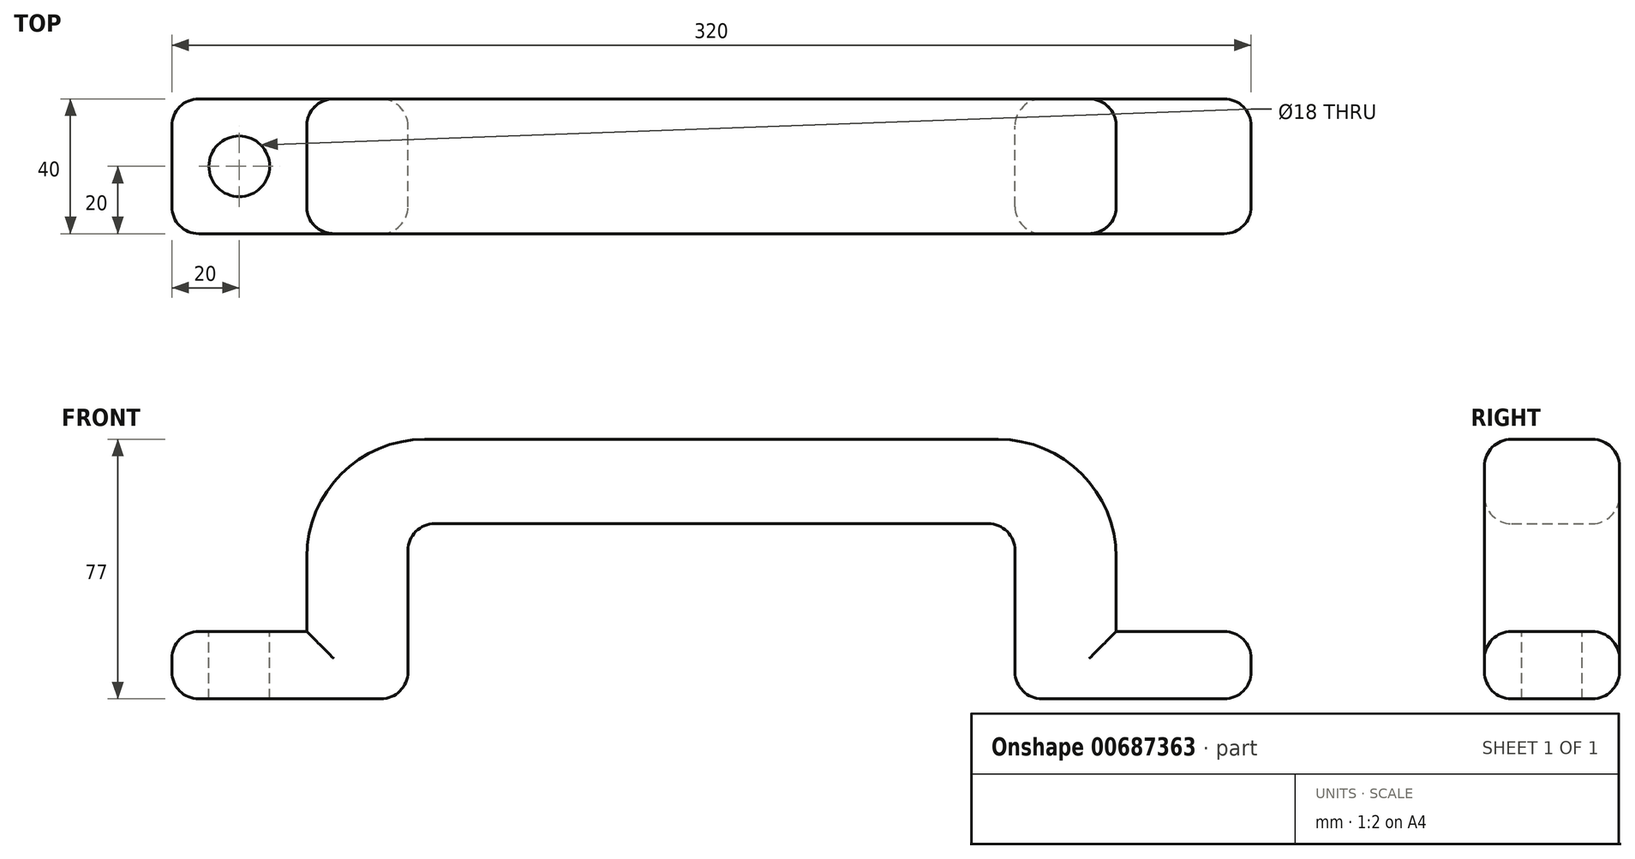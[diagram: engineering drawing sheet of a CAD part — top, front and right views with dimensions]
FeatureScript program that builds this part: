
annotation { "Feature Type Name" : "Feature", "Feature Type Description" : "" }
export const myFeature = defineFeature(function(context is Context, id is Id, definition is map)
    precondition{}
    {
        {
            var Q0;
            Q0=qCreatedBy(makeId("Front.planeOp"),FACE);
            var sketch = newSketch(context, id + "F0", { "sketchPlane" : qUnion([Q0])});
            skLineSegment(sketch, "E0.top", {"start": v(-120, 0) * mm, "end": v(-90, 0) * mm});
            skLineSegment(sketch, "E0.left", {"start": v(-120, 52) * mm, "end": v(-120, 0) * mm});
            skLineSegment(sketch, "E0.right", {"start": v(-90, 52) * mm, "end": v(-90, 0) * mm});
            skLineSegment(sketch, "E1.bottom", {"start": v(-90, 52) * mm, "end": v(0, 52) * mm});
            skLineSegment(sketch, "E1.top", {"start": v(-120, 77) * mm, "end": v(0, 77) * mm});
            skLineSegment(sketch, "E1.left", {"start": v(-120, 52) * mm, "end": v(-120, 77) * mm});
            skLineSegment(sketch, "E2.bottom", {"start": v(-120, 20) * mm, "end": v(-160, 20) * mm});
            skLineSegment(sketch, "E2.top", {"start": v(-120, 0) * mm, "end": v(-160, 0) * mm});
            skLineSegment(sketch, "E2.right", {"start": v(-160, 20) * mm, "end": v(-160, 0) * mm});
            skLineSegment(sketch, "E3.MirrorCS", {"start": v(120, 77) * mm, "end": v(0, 77) * mm});
            skLineSegment(sketch, "E4.MirrorCS", {"start": v(90, 52) * mm, "end": v(90, 0) * mm});
            skLineSegment(sketch, "E5.MirrorCS", {"start": v(120, 0) * mm, "end": v(90, 0) * mm});
            skLineSegment(sketch, "E6.MirrorCS", {"start": v(120, 0) * mm, "end": v(160, 0) * mm});
            skLineSegment(sketch, "E7.MirrorCS", {"start": v(160, 20) * mm, "end": v(160, 0) * mm});
            skLineSegment(sketch, "E8.MirrorCS", {"start": v(120, 52) * mm, "end": v(120, 20) * mm});
            skLineSegment(sketch, "E9.MirrorCS", {"start": v(120, 52) * mm, "end": v(120, 77) * mm});
            skLineSegment(sketch, "E10.MirrorCS", {"start": v(120, 20) * mm, "end": v(160, 20) * mm});
            skLineSegment(sketch, "E11.MirrorCS", {"start": v(90, 52) * mm, "end": v(0, 52) * mm});
            skPoint(sketch, "E12.orphan", {"position": v(120, 0) * mm});
            skSolve(sketch);
        }
        {
            var Q0;
            Q0 = qSketchRegion(id + "F0", true);
            extrude(context, id + "F1", {"entities" : qUnion([Q0]), "depth" : 40 * mm, "offsetDistance" : 25 * mm});
        }
        {
            var Q0;
            Q0=makeQuery(id+"F1.opExtrude","SWEPT_FACE",FACE,{"disambiguationData":[OSD([sQuery(id+"F0.wireOp",EDGE,"E2.bottom")])]});
            var sketch = newSketch(context, id + "F2", { "sketchPlane" : qUnion([Q0])});
            skCircle(sketch, "E13", {"center": v(-140, -20) * mm, "radius": 9 * mm});
            skPoint(sketch, "E13.centerSnap0", {"position": v(-140, 0) * mm});
            skPoint(sketch, "E13.centerSnap1", {"position": v(-120, -20) * mm});
            skSolve(sketch);
        }
        {
            var Q0;
            Q0 = qSketchRegion(id + "F2", true);
            extrude(context, id + "F3", {"entities" : qUnion([Q0]), "operationType" : NewBodyOperationType.REMOVE, "oppositeDirection" : true, "depth" : 74.7 * mm, "offsetDistance" : 25 * mm});
        }
        {
            var Q0;
            Q0=makeQuery(id+"F1.opExtrude","CAP_EDGE",EDGE,{"disambiguationData":[OSD([sQuery(id+"F0.wireOp",EDGE,"E2.right")])],"isStart":false});
            var Q1;
            Q1=makeQuery(id+"F1.opExtrude","CAP_EDGE",EDGE,{"disambiguationData":[OSD([sQuery(id+"F0.wireOp",EDGE,"E2.right")])],"isStart":true});
            var Q2;
            Q2=makeQuery(id+"F1.opExtrude","CAP_EDGE",EDGE,{"disambiguationData":[OSD([sQuery(id+"F0.wireOp",EDGE,"E7.MirrorCS")])],"isStart":true});
            var Q3;
            Q3=makeQuery(id+"F1.opExtrude","CAP_EDGE",EDGE,{"disambiguationData":[OSD([sQuery(id+"F0.wireOp",EDGE,"E7.MirrorCS")])],"isStart":false});
            var Q4;
            Q4=makeQuery(id+"F1.opExtrude","CAP_EDGE",EDGE,{"disambiguationData":[OSD([sQuery(id+"F0.wireOp",EDGE,"E10.MirrorCS")])],"isStart":true});
            var Q5;
            Q5=makeQuery(id+"F1.opExtrude","CAP_EDGE",EDGE,{"disambiguationData":[OSD([sQuery(id+"F0.wireOp",EDGE,"E8.MirrorCS"),sQuery(id+"F0.wireOp",EDGE,"E9.MirrorCS")])],"isStart":true});
            var Q6;
            Q6=makeQuery(id+"F1.opExtrude","CAP_EDGE",EDGE,{"disambiguationData":[OSD([sQuery(id+"F0.wireOp",EDGE,"E1.top"),sQuery(id+"F0.wireOp",EDGE,"E3.MirrorCS")])],"isStart":true});
            var Q7;
            Q7=makeQuery(id+"F1.opExtrude","CAP_EDGE",EDGE,{"disambiguationData":[OSD([sQuery(id+"F0.wireOp",EDGE,"E0.left"),sQuery(id+"F0.wireOp",EDGE,"E1.left")])],"isStart":true});
            var Q8;
            Q8=makeQuery(id+"F1.opExtrude","CAP_EDGE",EDGE,{"disambiguationData":[OSD([sQuery(id+"F0.wireOp",EDGE,"E2.bottom")])],"isStart":true});
            var Q9;
            Q9=makeQuery(id+"F1.opExtrude","CAP_EDGE",EDGE,{"disambiguationData":[OSD([sQuery(id+"F0.wireOp",EDGE,"E2.bottom")])],"isStart":false});
            var Q10;
            Q10=makeQuery(id+"F1.opExtrude","CAP_EDGE",EDGE,{"disambiguationData":[OSD([sQuery(id+"F0.wireOp",EDGE,"E0.left"),sQuery(id+"F0.wireOp",EDGE,"E1.left")])],"isStart":false});
            var Q11;
            Q11=makeQuery(id+"F1.opExtrude","CAP_EDGE",EDGE,{"disambiguationData":[OSD([sQuery(id+"F0.wireOp",EDGE,"E1.top"),sQuery(id+"F0.wireOp",EDGE,"E3.MirrorCS")])],"isStart":false});
            var Q12;
            Q12=makeQuery(id+"F1.opExtrude","CAP_EDGE",EDGE,{"disambiguationData":[OSD([sQuery(id+"F0.wireOp",EDGE,"E8.MirrorCS"),sQuery(id+"F0.wireOp",EDGE,"E9.MirrorCS")])],"isStart":false});
            var Q13;
            Q13=makeQuery(id+"F1.opExtrude","CAP_EDGE",EDGE,{"disambiguationData":[OSD([sQuery(id+"F0.wireOp",EDGE,"E10.MirrorCS")])],"isStart":false});
            var Q14;
            Q14=makeQuery(id+"F1.opExtrude","SWEPT_EDGE",EDGE,{"disambiguationData":[OSD([sQuery(id+"F0.wireOp",EDGE,"E7.MirrorCS"),sQuery(id+"F0.wireOp",EDGE,"E10.MirrorCS")])]});
            var Q15;
            Q15=makeQuery(id+"F1.opExtrude","SWEPT_EDGE",EDGE,{"disambiguationData":[OSD([sQuery(id+"F0.wireOp",EDGE,"E6.MirrorCS"),sQuery(id+"F0.wireOp",EDGE,"E7.MirrorCS")])]});
            var Q16;
            Q16=makeQuery(id+"F1.opExtrude","CAP_EDGE",EDGE,{"disambiguationData":[OSD([sQuery(id+"F0.wireOp",EDGE,"E4.MirrorCS")])],"isStart":true});
            var Q17;
            Q17=makeQuery(id+"F1.opExtrude","CAP_EDGE",EDGE,{"disambiguationData":[OSD([sQuery(id+"F0.wireOp",EDGE,"E1.bottom"),sQuery(id+"F0.wireOp",EDGE,"E11.MirrorCS")])],"isStart":true});
            var Q18;
            Q18=makeQuery(id+"F1.opExtrude","CAP_EDGE",EDGE,{"disambiguationData":[OSD([sQuery(id+"F0.wireOp",EDGE,"E0.right")])],"isStart":true});
            var Q19;
            Q19=makeQuery(id+"F1.opExtrude","CAP_EDGE",EDGE,{"disambiguationData":[OSD([sQuery(id+"F0.wireOp",EDGE,"E0.top"),sQuery(id+"F0.wireOp",EDGE,"E2.top")])],"isStart":true});
            var Q20;
            Q20=makeQuery(id+"F1.opExtrude","SWEPT_EDGE",EDGE,{"disambiguationData":[OSD([sQuery(id+"F0.wireOp",EDGE,"E2.top"),sQuery(id+"F0.wireOp",EDGE,"E2.right")])]});
            var Q21;
            Q21=makeQuery(id+"F1.opExtrude","CAP_EDGE",EDGE,{"disambiguationData":[OSD([sQuery(id+"F0.wireOp",EDGE,"E0.top"),sQuery(id+"F0.wireOp",EDGE,"E2.top")])],"isStart":false});
            var Q22;
            Q22=makeQuery(id+"F1.opExtrude","CAP_EDGE",EDGE,{"disambiguationData":[OSD([sQuery(id+"F0.wireOp",EDGE,"E0.right")])],"isStart":false});
            var Q23;
            Q23=makeQuery(id+"F1.opExtrude","CAP_EDGE",EDGE,{"disambiguationData":[OSD([sQuery(id+"F0.wireOp",EDGE,"E1.bottom"),sQuery(id+"F0.wireOp",EDGE,"E11.MirrorCS")])],"isStart":false});
            var Q24;
            Q24=makeQuery(id+"F1.opExtrude","CAP_EDGE",EDGE,{"disambiguationData":[OSD([sQuery(id+"F0.wireOp",EDGE,"E4.MirrorCS")])],"isStart":false});
            var Q25;
            Q25=makeQuery(id+"F1.opExtrude","CAP_EDGE",EDGE,{"disambiguationData":[OSD([sQuery(id+"F0.wireOp",EDGE,"E5.MirrorCS"),sQuery(id+"F0.wireOp",EDGE,"E6.MirrorCS")])],"isStart":false});
            var Q26;
            Q26=makeQuery(id+"F1.opExtrude","SWEPT_EDGE",EDGE,{"disambiguationData":[OSD([sQuery(id+"F0.wireOp",EDGE,"E4.MirrorCS"),sQuery(id+"F0.wireOp",EDGE,"E5.MirrorCS")])]});
            var Q27;
            Q27=makeQuery(id+"F1.opExtrude","SWEPT_EDGE",EDGE,{"disambiguationData":[OSD([sQuery(id+"F0.wireOp",EDGE,"E4.MirrorCS"),sQuery(id+"F0.wireOp",EDGE,"E11.MirrorCS")])]});
            var Q28;
            Q28=makeQuery(id+"F1.opExtrude","SWEPT_EDGE",EDGE,{"disambiguationData":[OSD([sQuery(id+"F0.wireOp",EDGE,"E0.right"),sQuery(id+"F0.wireOp",EDGE,"E1.bottom")])]});
            var Q29;
            Q29=makeQuery(id+"F1.opExtrude","SWEPT_EDGE",EDGE,{"disambiguationData":[OSD([sQuery(id+"F0.wireOp",EDGE,"E2.bottom"),sQuery(id+"F0.wireOp",EDGE,"E2.right")])]});
            var Q30;
            Q30=makeQuery(id+"F1.opExtrude","CAP_EDGE",EDGE,{"disambiguationData":[OSD([sQuery(id+"F0.wireOp",EDGE,"E5.MirrorCS"),sQuery(id+"F0.wireOp",EDGE,"E6.MirrorCS")])],"isStart":true});
            var Q31;
            Q31=makeQuery(id+"F1.opExtrude","SWEPT_EDGE",EDGE,{"disambiguationData":[OSD([sQuery(id+"F0.wireOp",EDGE,"E0.top"),sQuery(id+"F0.wireOp",EDGE,"E0.right")])]});
            fillet(context, id + "F4", {"entities" : qUnion([Q0, Q1, Q2, Q3, Q4, Q5, Q6, Q7, Q8, Q9, Q10, Q11, Q12, Q13, Q14, Q15, Q16, Q17, Q18, Q19, Q20, Q21, Q22, Q23, Q24, Q25, Q26, Q27, Q28, Q29, Q30, Q31]), "radius" : 8 * mm, "tangentPropagation" : true, "allowEdgeOverflow" : false});
        }
        {
            var Q0;
            Q0=makeQuery(id+"F1.opExtrude","SWEPT_EDGE",EDGE,{"disambiguationData":[OSD([sQuery(id+"F0.wireOp",EDGE,"E1.top"),sQuery(id+"F0.wireOp",EDGE,"E1.left")])]});
            var Q1;
            Q1=makeQuery(id+"F1.opExtrude","SWEPT_EDGE",EDGE,{"disambiguationData":[OSD([sQuery(id+"F0.wireOp",EDGE,"E3.MirrorCS"),sQuery(id+"F0.wireOp",EDGE,"E9.MirrorCS")])]});
            fillet(context, id + "F5", {"entities" : qUnion([Q0, Q1]), "radius" : 35 * mm, "tangentPropagation" : true, "allowEdgeOverflow" : false});
        }
    });
